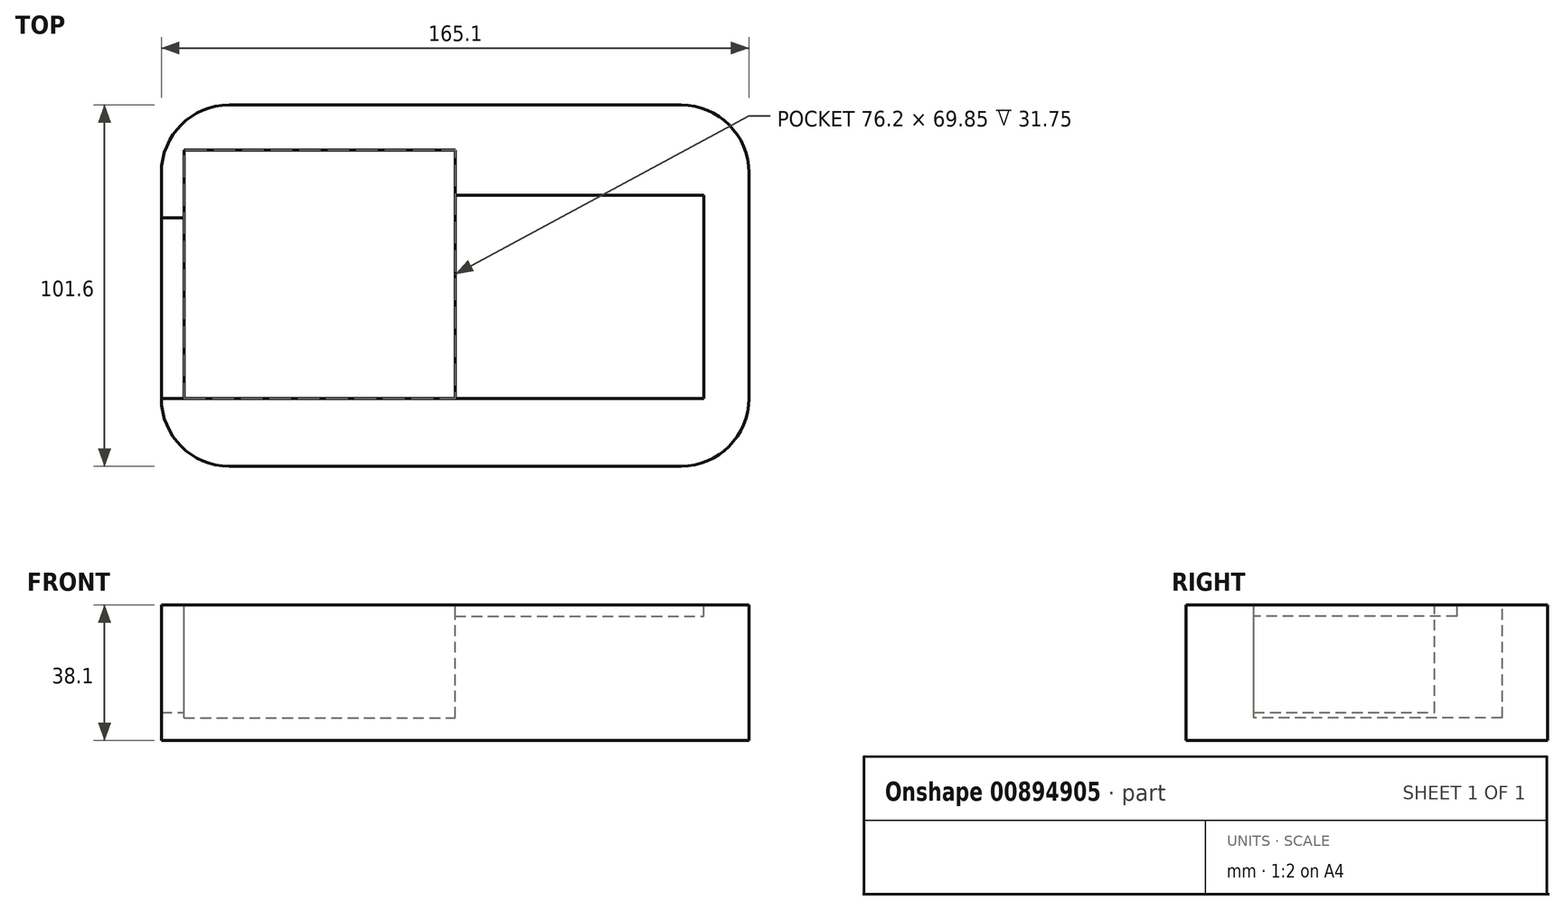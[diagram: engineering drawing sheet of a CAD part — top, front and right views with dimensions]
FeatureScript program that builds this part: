
annotation { "Feature Type Name" : "Feature", "Feature Type Description" : "" }
export const myFeature = defineFeature(function(context is Context, id is Id, definition is map)
    precondition{}
    {
        {
            var Q0;
            Q0=qCreatedBy(makeId("Front.planeOp"),FACE);
            var sketch = newSketch(context, id + "F0", { "sketchPlane" : qUnion([Q0])});
            skLineSegment(sketch, "E0.bottom", {"start": v(-105.45, 11.52) * mm, "end": v(59.65, 11.52) * mm});
            skLineSegment(sketch, "E0.top", {"start": v(-105.45, -26.58) * mm, "end": v(59.65, -26.58) * mm});
            skLineSegment(sketch, "E0.left", {"start": v(-105.45, 11.52) * mm, "end": v(-105.45, -26.58) * mm});
            skLineSegment(sketch, "E0.right", {"start": v(59.65, 11.52) * mm, "end": v(59.65, -26.58) * mm});
            skSolve(sketch);
        }
        {
            var Q0;
            Q0=makeQuery(id+"F0.imprint","IMPRINT",FACE,{"disambiguationData":[TD([[makeQuery(id+"F0.imprint","IMPRINT",EDGE,{"derivedFrom":sQuery(id+"F0.wireOp",EDGE,"E0.bottom")}),-1.0]])]});
            extrude(context, id + "F1", {"entities" : qUnion([Q0]), "endBound" : BoundingType.SYMMETRIC, "depth" : 101.6 * mm, "offsetDistance" : 25.4 * mm});
        }
        {
            var Q0;
            Q0=makeQuery(id+"F1.opExtrude","SWEPT_FACE",FACE,{"disambiguationData":[OSD([sQuery(id+"F0.wireOp",EDGE,"E0.bottom")])]});
            var sketch = newSketch(context, id + "F2", { "sketchPlane" : qUnion([Q0])});
            skLineSegment(sketch, "E1.bottom", {"start": v(-99.1, 38.1) * mm, "end": v(-22.9, 38.1) * mm});
            skLineSegment(sketch, "E1.top", {"start": v(-99.1, -31.75) * mm, "end": v(-22.9, -31.75) * mm});
            skLineSegment(sketch, "E1.left", {"start": v(-99.1, 38.1) * mm, "end": v(-99.1, -31.75) * mm});
            skLineSegment(sketch, "E1.right", {"start": v(-22.9, 38.1) * mm, "end": v(-22.9, -31.75) * mm});
            skSolve(sketch);
        }
        {
            var Q0;
            Q0 = qSketchRegion(id + "F2", true);
            extrude(context, id + "F3", {"entities" : qUnion([Q0]), "operationType" : NewBodyOperationType.REMOVE, "oppositeDirection" : true, "depth" : 31.75 * mm, "offsetDistance" : 25.4 * mm});
        }
        {
            var Q0;
            Q0=makeQuery(id+"F1.opExtrude","SWEPT_FACE",FACE,{"disambiguationData":[OSD([sQuery(id+"F0.wireOp",EDGE,"E0.bottom")])]});
            var sketch = newSketch(context, id + "F4", { "sketchPlane" : qUnion([Q0])});
            skSolve(sketch);
        }
        {
            var Q0;
            {var subQ0=sQuery(id+"F0.wireOp",EDGE,"E0.bottom");Q0=makeQuery(id+"F4.imprint","IMPRINT",FACE,{"disambiguationData":[TD([[makeQuery(id+"F4.imprint","IMPRINT",EDGE,{"derivedFrom":makeQuery(id+"F1.opExtrude","CAP_EDGE",EDGE,{"disambiguationData":[OSD([subQ0])],"isStart":true})}),-1.0]])]});}
            var sketch = newSketch(context, id + "F5", { "sketchPlane" : qUnion([Q0])});
            skLineSegment(sketch, "E2.bottom", {"start": v(-105.45, 19.05) * mm, "end": v(-99.1, 19.05) * mm});
            skLineSegment(sketch, "E2.top", {"start": v(-105.45, -31.75) * mm, "end": v(-99.1, -31.75) * mm});
            skLineSegment(sketch, "E2.left", {"start": v(-105.45, 19.05) * mm, "end": v(-105.45, -31.75) * mm});
            skLineSegment(sketch, "E2.right", {"start": v(-99.1, 19.05) * mm, "end": v(-99.1, -31.75) * mm});
            skSolve(sketch);
        }
        {
            var Q0;
            Q0=makeQuery(id+"F5.imprint","IMPRINT",FACE,{"disambiguationData":[TD([[makeQuery(id+"F5.imprint","IMPRINT",EDGE,{"derivedFrom":sQuery(id+"F5.wireOp",EDGE,"E2.bottom")}),-1.0]])]});
            extrude(context, id + "F6", {"entities" : qUnion([Q0]), "operationType" : NewBodyOperationType.REMOVE, "oppositeDirection" : true, "depth" : 30.16 * mm, "offsetDistance" : 25.4 * mm});
        }
        {
            var Q0;
            {var subQ0=sQuery(id+"F0.wireOp",EDGE,"E0.bottom");Q0=makeQuery(id+"F4.imprint","IMPRINT",FACE,{"disambiguationData":[TD([[makeQuery(id+"F4.imprint","IMPRINT",EDGE,{"derivedFrom":makeQuery(id+"F1.opExtrude","CAP_EDGE",EDGE,{"disambiguationData":[OSD([subQ0])],"isStart":true})}),-1.0]])]});}
            var sketch = newSketch(context, id + "F7", { "sketchPlane" : qUnion([Q0])});
            skLineSegment(sketch, "E3.bottom", {"start": v(-22.9, -31.75) * mm, "end": v(46.95, -31.75) * mm});
            skLineSegment(sketch, "E3.top", {"start": v(-22.9, 25.4) * mm, "end": v(46.95, 25.4) * mm});
            skLineSegment(sketch, "E3.left", {"start": v(-22.9, -31.75) * mm, "end": v(-22.9, 25.4) * mm});
            skLineSegment(sketch, "E3.right", {"start": v(46.95, -31.75) * mm, "end": v(46.95, 25.4) * mm});
            skSolve(sketch);
        }
        {
            var Q0;
            Q0 = qSketchRegion(id + "F7", true);
            extrude(context, id + "F8", {"entities" : qUnion([Q0]), "operationType" : NewBodyOperationType.REMOVE, "oppositeDirection" : true, "depth" : 3.17 * mm, "offsetDistance" : 25.4 * mm});
        }
        {
            var Q0;
            Q0=makeQuery(id+"F1.opExtrude","CAP_EDGE",EDGE,{"disambiguationData":[OSD([sQuery(id+"F0.wireOp",EDGE,"E0.left")])],"isStart":false});
            fillet(context, id + "F9", {"entities" : qUnion([Q0]), "radius" : 19.05 * mm, "tangentPropagation" : true, "allowEdgeOverflow" : false});
        }
        {
            var Q0;
            Q0=makeQuery(id+"F1.opExtrude","CAP_EDGE",EDGE,{"disambiguationData":[OSD([sQuery(id+"F0.wireOp",EDGE,"E0.right")])],"isStart":false});
            fillet(context, id + "F10", {"entities" : qUnion([Q0]), "radius" : 19.05 * mm, "tangentPropagation" : true, "allowEdgeOverflow" : false});
        }
        {
            var Q0;
            Q0=makeQuery(id+"F1.opExtrude","CAP_EDGE",EDGE,{"disambiguationData":[OSD([sQuery(id+"F0.wireOp",EDGE,"E0.right")])],"isStart":true});
            var Q1;
            Q1=makeQuery(id+"F1.opExtrude","CAP_EDGE",EDGE,{"disambiguationData":[OSD([sQuery(id+"F0.wireOp",EDGE,"E0.left")])],"isStart":true});
            fillet(context, id + "F11", {"entities" : qUnion([Q0, Q1]), "radius" : 19.05 * mm, "tangentPropagation" : true, "allowEdgeOverflow" : false});
        }
    });
